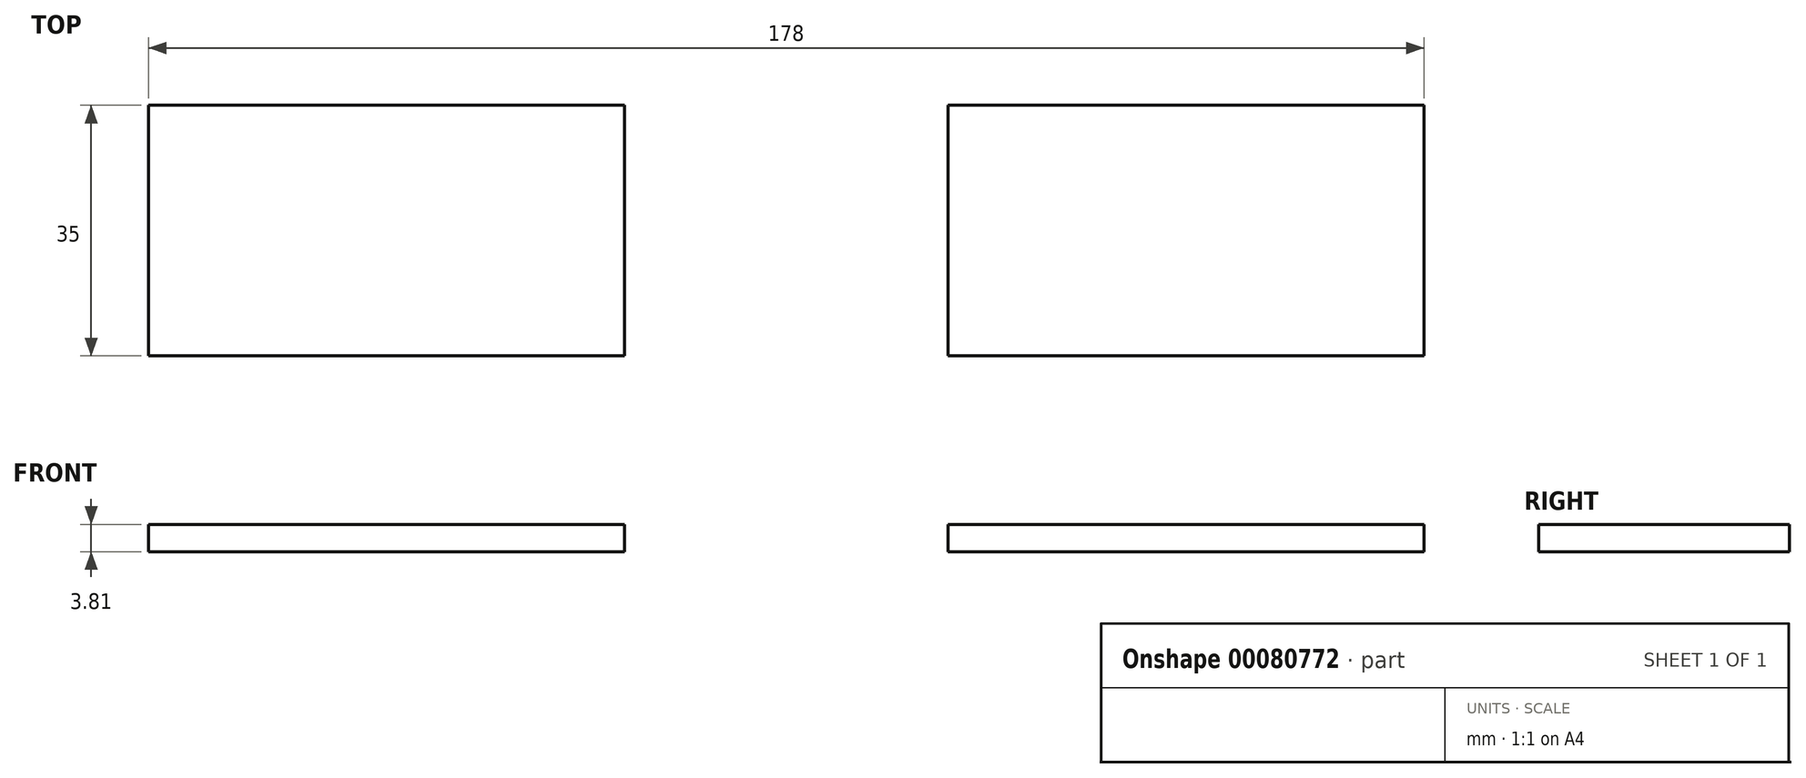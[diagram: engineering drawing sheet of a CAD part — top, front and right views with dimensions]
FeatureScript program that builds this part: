
annotation { "Feature Type Name" : "Feature", "Feature Type Description" : "" }
export const myFeature = defineFeature(function(context is Context, id is Id, definition is map)
    precondition{}
    {
        {
            var Q0;
            Q0=qCreatedBy(makeId("Top.planeOp"),FACE);
            var sketch = newSketch(context, id + "F0", { "sketchPlane" : qUnion([Q0])});
            skLineSegment(sketch, "E0.bottom", {"start": v(89, 17.5) * mm, "end": v(-89, 17.5) * mm});
            skLineSegment(sketch, "E0.top", {"start": v(89, -17.5) * mm, "end": v(-89, -17.5) * mm});
            skLineSegment(sketch, "E0.left", {"start": v(89, 17.5) * mm, "end": v(89, -17.5) * mm});
            skLineSegment(sketch, "E0.right", {"start": v(-89, 17.5) * mm, "end": v(-89, -17.5) * mm});
            skPoint(sketch, "E0.middle", {"position": v(0, 0) * mm});
            skLineSegment(sketch, "E1", {"start": v(-22.58, 17.5) * mm, "end": v(-22.58, -17.5) * mm});
            skLineSegment(sketch, "E2", {"start": v(0, 17.5) * mm, "end": v(0, -17.5) * mm});
            skLineSegment(sketch, "E3.MirrorCS", {"start": v(22.58, 17.5) * mm, "end": v(22.58, -17.5) * mm});
            skSolve(sketch);
        }
        {
            var Q0;
            {var subQ3=sQuery(id+"F0.wireOp",EDGE,"E0.right");Q0=makeQuery(id+"F0.imprint","IMPRINT",FACE,{"disambiguationData":[TD([[makeQuery(id+"F0.imprint","IMPRINT",EDGE,{"derivedFrom":subQ3}),1.0]])]});}
            var Q1;
            {var subQ0=sQuery(id+"F0.wireOp",EDGE,"cI3HY2o2-Qt3k-GyWe-tqof-2Gcz2GmZ4jtz");Q1=makeQuery(id+"F0.imprint","IMPRINT",FACE,{"disambiguationData":[TD([[makeQuery(id+"F0.imprint","IMPRINT",EDGE,{"derivedFrom":subQ0}),1.0]])]});}
            var Q2;
            {var subQ0=sQuery(id+"F0.wireOp",EDGE,"zidLMQz6-Q9wf-yULA-voi1-l9MzTruIfwaP");Q2=makeQuery(id+"F0.imprint","IMPRINT",FACE,{"disambiguationData":[TD([[makeQuery(id+"F0.imprint","IMPRINT",EDGE,{"derivedFrom":subQ0}),1.0]])]});}
            var Q3;
            {var subQ4=sQuery(id+"F0.wireOp",EDGE,"E0.left");Q3=makeQuery(id+"F0.imprint","IMPRINT",FACE,{"disambiguationData":[TD([[makeQuery(id+"F0.imprint","IMPRINT",EDGE,{"derivedFrom":subQ4}),-1.0]])]});}
            var Q4;
            {var subQ0=sQuery(id+"F0.wireOp",EDGE,"ec3eca7a-1bbd-497a-9b17-b1af3d44a4700.MirrorCS");Q4=makeQuery(id+"F0.imprint","IMPRINT",FACE,{"disambiguationData":[TD([[makeQuery(id+"F0.imprint","IMPRINT",EDGE,{"derivedFrom":subQ0}),-1.0]])]});}
            var Q5;
            {var subQ0=sQuery(id+"F0.wireOp",EDGE,"22e142fa-472f-43a1-8ab7-730ca1003af10.MirrorCS");Q5=makeQuery(id+"F0.imprint","IMPRINT",FACE,{"disambiguationData":[TD([[makeQuery(id+"F0.imprint","IMPRINT",EDGE,{"derivedFrom":subQ0}),-1.0]])]});}
            extrude(context, id + "F1", {"entities" : qUnion([Q0, Q1, Q2, Q3, Q4, Q5]), "depth" : 3.8 * mm});
        }
    });
